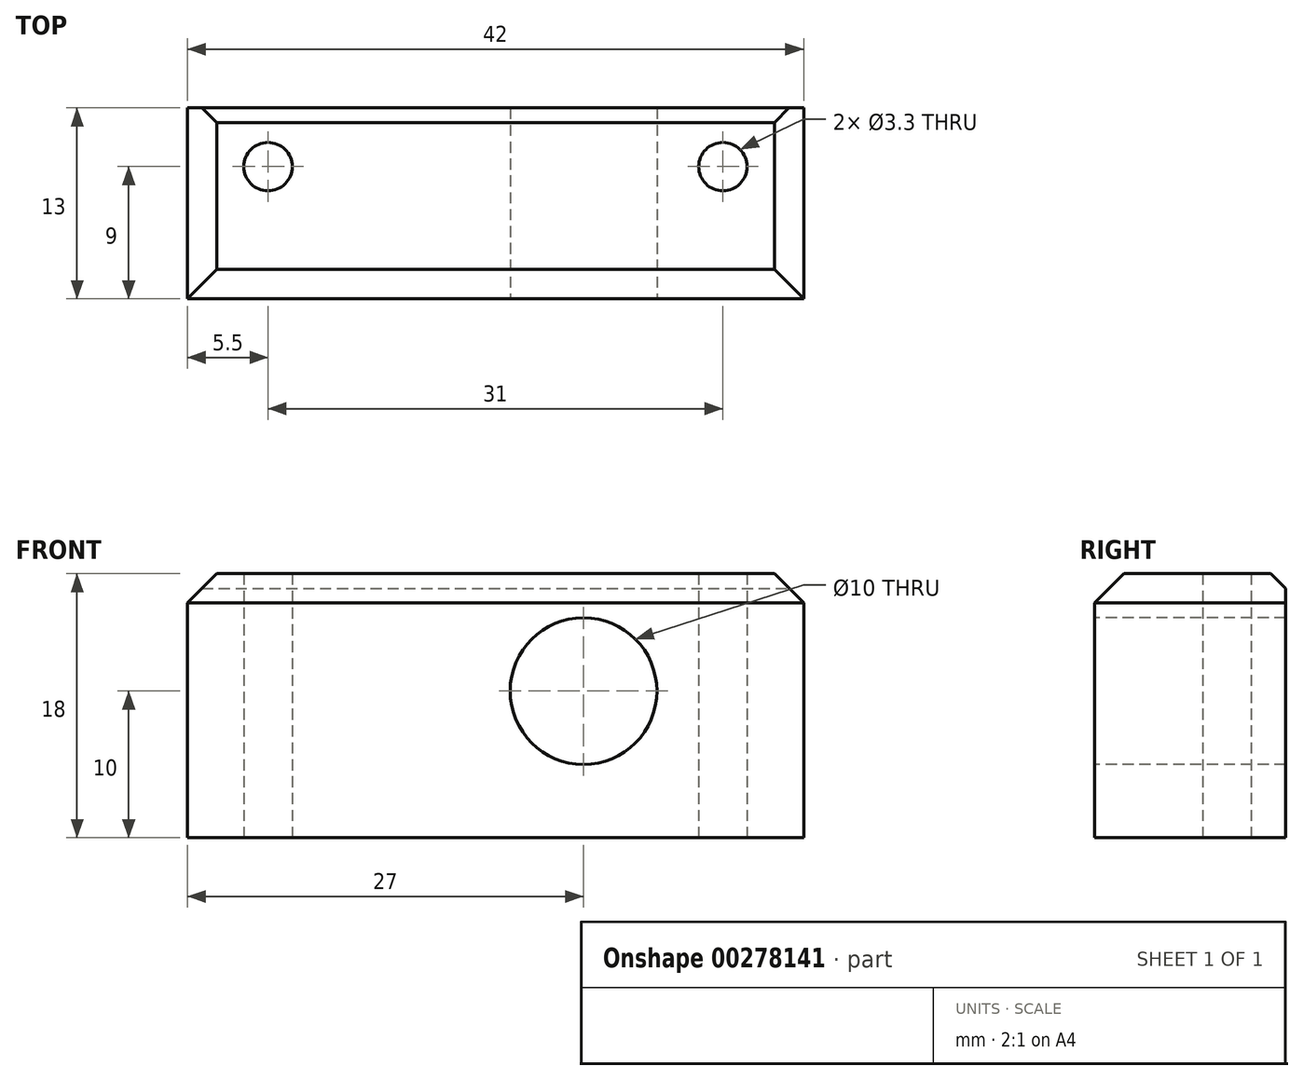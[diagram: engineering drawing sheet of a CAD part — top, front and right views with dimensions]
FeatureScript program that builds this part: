
annotation { "Feature Type Name" : "Feature", "Feature Type Description" : "" }
export const myFeature = defineFeature(function(context is Context, id is Id, definition is map)
    precondition{}
    {
        {
            var Q0;
            Q0=qCreatedBy(makeId("Top.planeOp"),FACE);
            var sketch = newSketch(context, id + "F0", { "sketchPlane" : qUnion([Q0])});
            skLineSegment(sketch, "E0.bottom", {"start": v(-21, 6.5) * mm, "end": v(21, 6.5) * mm});
            skLineSegment(sketch, "E0.top", {"start": v(-21, -6.5) * mm, "end": v(21, -6.5) * mm});
            skLineSegment(sketch, "E0.left", {"start": v(-21, 6.5) * mm, "end": v(-21, -6.5) * mm});
            skLineSegment(sketch, "E0.right", {"start": v(21, 6.5) * mm, "end": v(21, -6.5) * mm});
            skPoint(sketch, "E0.middle", {"position": v(0, 0) * mm});
            skCircle(sketch, "E1", {"center": v(-15.5, 2.5) * mm, "radius": 1.65 * mm});
            skCircle(sketch, "E2", {"center": v(15.5, 2.5) * mm, "radius": 1.65 * mm});
            skSolve(sketch);
        }
        {
            var Q0;
            Q0=makeQuery(id+"F0.imprint","IMPRINT",FACE,{"disambiguationData":[TD([[makeQuery(id+"F0.imprint","IMPRINT",EDGE,{"derivedFrom":sQuery(id+"F0.wireOp",EDGE,"E0.bottom")}),-1.0]])]});
            extrude(context, id + "F1", {"entities" : qUnion([Q0]), "depth" : 18 * mm});
        }
        {
            var Q0;
            Q0=makeQuery(id+"F1.opExtrude","SWEPT_FACE",FACE,{"disambiguationData":[OSD([sQuery(id+"F0.wireOp",EDGE,"E0.top")])]});
            var sketch = newSketch(context, id + "F2", { "sketchPlane" : qUnion([Q0])});
            skCircle(sketch, "E3", {"center": v(6, 10) * mm, "radius": 5 * mm});
            skSolve(sketch);
        }
        {
            var Q0;
            Q0=makeQuery(id+"F2.imprint","IMPRINT",FACE,{"disambiguationData":[TD([[makeQuery(id+"F2.imprint","IMPRINT",EDGE,{"derivedFrom":sQuery(id+"F2.wireOp",EDGE,"E3")}),1.0]])]});
            extrude(context, id + "F3", {"entities" : qUnion([Q0]), "operationType" : NewBodyOperationType.REMOVE, "endBound" : BoundingType.UP_TO_NEXT, "oppositeDirection" : true, "depth" : 25 * mm});
        }
        {
            var Q0;
            Q0=makeQuery(id+"F1.opExtrude","CAP_EDGE",EDGE,{"disambiguationData":[OSD([sQuery(id+"F0.wireOp",EDGE,"E0.left")])],"isStart":false});
            var Q1;
            Q1=makeQuery(id+"F1.opExtrude","CAP_EDGE",EDGE,{"disambiguationData":[OSD([sQuery(id+"F0.wireOp",EDGE,"E0.top")])],"isStart":false});
            var Q2;
            Q2=makeQuery(id+"F1.opExtrude","CAP_EDGE",EDGE,{"disambiguationData":[OSD([sQuery(id+"F0.wireOp",EDGE,"E0.right")])],"isStart":false});
            chamfer(context, id + "F4", {"entities" : qUnion([Q0, Q1, Q2]), "width" : 2 * mm, "tangentPropagation" : true});
        }
        {
            var Q0;
            Q0=makeQuery(id+"F1.opExtrude","CAP_EDGE",EDGE,{"disambiguationData":[OSD([sQuery(id+"F0.wireOp",EDGE,"E0.bottom")])],"isStart":false});
            chamfer(context, id + "F5", {"entities" : qUnion([Q0]), "width" : 1 * mm, "tangentPropagation" : true});
        }
    });
